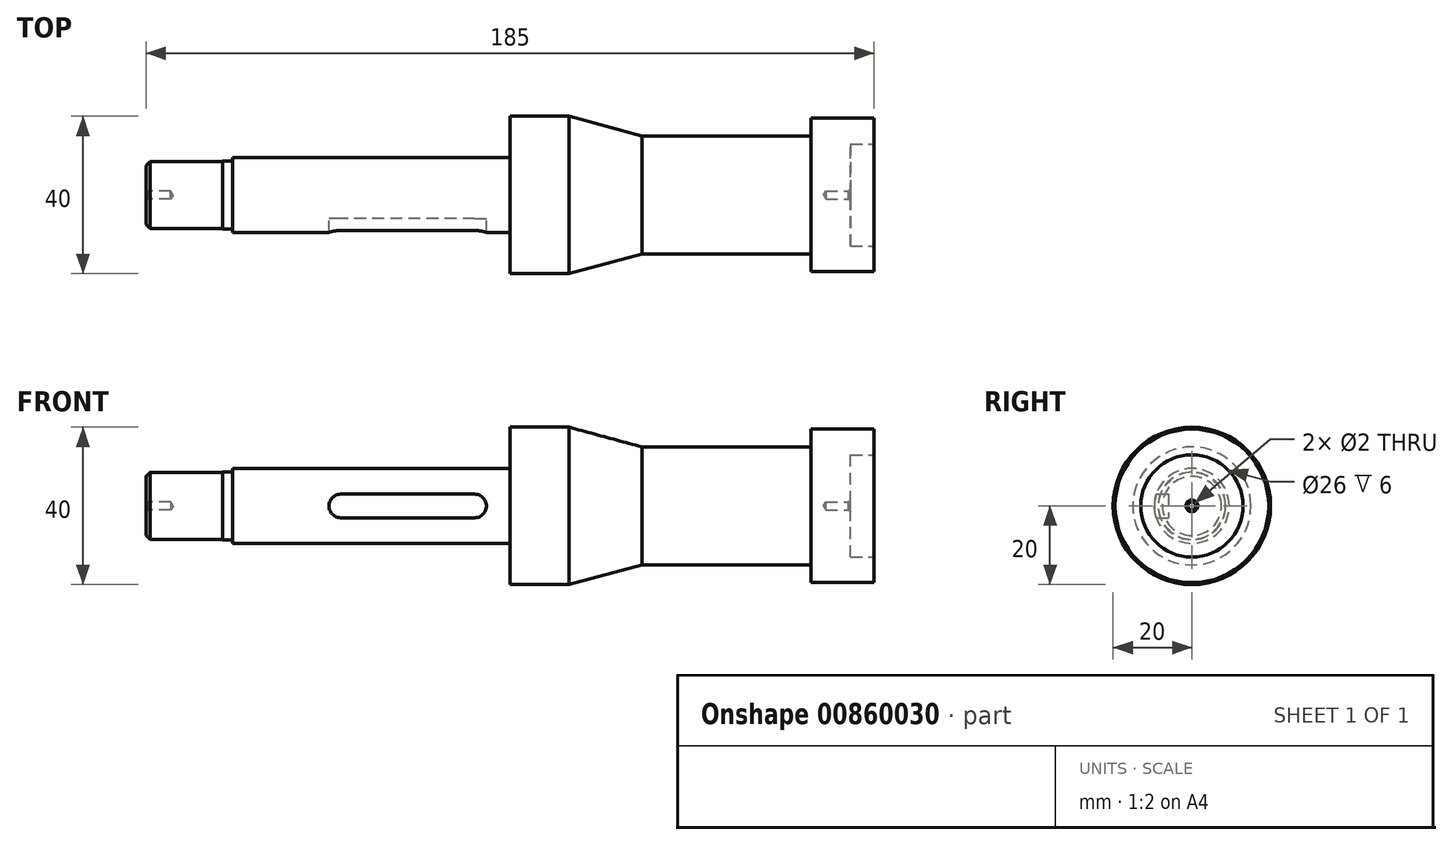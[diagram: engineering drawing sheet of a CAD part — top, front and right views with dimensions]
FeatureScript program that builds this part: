
annotation { "Feature Type Name" : "Feature", "Feature Type Description" : "" }
export const myFeature = defineFeature(function(context is Context, id is Id, definition is map)
    precondition{}
    {
        {
            var Q0;
            Q0=qCreatedBy(makeId("Front.planeOp"),FACE);
            var sketch = newSketch(context, id + "F0", { "sketchPlane" : qUnion([Q0])});
            skLineSegment(sketch, "E0", {"start": v(0, 7.5) * mm, "end": v(1, 8.5) * mm});
            skLineSegment(sketch, "E1", {"start": v(1, 8.5) * mm, "end": v(19.5, 8.5) * mm});
            skLineSegment(sketch, "E2", {"start": v(22, 8.5) * mm, "end": v(22, 9.5) * mm});
            skLineSegment(sketch, "E3", {"start": v(22, 9.5) * mm, "end": v(92.5, 9.5) * mm});
            skLineSegment(sketch, "E4", {"start": v(92.5, 9.5) * mm, "end": v(92.5, 20) * mm});
            skLineSegment(sketch, "E5", {"start": v(92.5, 20) * mm, "end": v(107.5, 20) * mm});
            skLineSegment(sketch, "E6", {"start": v(107.5, 20) * mm, "end": v(126, 15) * mm});
            skLineSegment(sketch, "E7", {"start": v(126, 15) * mm, "end": v(169, 15) * mm});
            skLineSegment(sketch, "E8", {"start": v(169, 15) * mm, "end": v(169, 0) * mm});
            skLineSegment(sketch, "E9", {"start": v(169, 0) * mm, "end": v(0, 0) * mm});
            skLineSegment(sketch, "E10", {"start": v(0, 7.5) * mm, "end": v(0, 0) * mm});
            skLineSegment(sketch, "E11", {"start": v(0, 0) * mm, "end": v(210.6, 0) * mm, "construction": true});
            skLineSegment(sketch, "E12", {"start": v(169, 15) * mm, "end": v(169, 19.5) * mm});
            skLineSegment(sketch, "E13", {"start": v(169, 19.5) * mm, "end": v(185, 19.5) * mm});
            skLineSegment(sketch, "E14", {"start": v(185, 19.5) * mm, "end": v(185, 0) * mm});
            skLineSegment(sketch, "E15", {"start": v(185, 0) * mm, "end": v(169, 0) * mm});
            skLineSegment(sketch, "E16", {"start": v(19.5, 8.5) * mm, "end": v(19.5, 8.6) * mm});
            skLineSegment(sketch, "E17", {"start": v(19.5, 8.6) * mm, "end": v(22, 8.6) * mm});
            skSolve(sketch);
        }
        {
            var Q0;
            Q0 = qSketchRegion(id + "F0", true);
            var Q1;
            Q1=sQuery(id+"F0.wireOp",EDGE,"E11");
            revolve(context, id + "F1", {"surfaceOperationType" : NewSurfaceOperationType.NEW, "entities" : qUnion([Q0]), "axis" : qUnion([Q1]), "revolveType" : RevolveType.FULL});
        }
        {
            var Q0;
            Q0=qCreatedBy(makeId("Front.planeOp"),FACE);
            var sketch = newSketch(context, id + "F2", { "sketchPlane" : qUnion([Q0])});
            skLineSegment(sketch, "E18.bottom", {"start": v(83.5, 3) * mm, "end": v(49.5, 3) * mm});
            skLineSegment(sketch, "E18.top", {"start": v(83.5, -3) * mm, "end": v(49.5, -3) * mm});
            skPoint(sketch, "E18.middle", {"position": v(66.5, 0) * mm});
            skArc(sketch, "E19", {"start": v(49.5, 3) * mm, "mid": v(46.5, 0) * mm, "end": v(49.5, -3) * mm});
            skArc(sketch, "E20", {"start": v(83.5, -3) * mm, "mid": v(86.5, 0) * mm, "end": v(83.5, 3) * mm});
            skSolve(sketch);
        }
        {
            var Q0;
            Q0 = qSketchRegion(id + "F2", true);
            extrude(context, id + "F3", {"entities" : qUnion([Q0]), "operationType" : NewBodyOperationType.REMOVE, "depth" : 15.4 * mm, "offsetDistance" : 25 * mm, "hasSecondDirection" : true, "secondDirectionOppositeDirection" : false, "secondDirectionDepth" : 6 * mm});
        }
        {
            var Q0;
            Q0=makeQuery(id+"F1.opRevolve","SWEPT_FACE",FACE,{"disambiguationData":[OSD([sQuery(id+"F0.wireOp",EDGE,"E14")])]});
            var sketch = newSketch(context, id + "F4", { "sketchPlane" : qUnion([Q0])});
            skCircle(sketch, "E21", {"center": v(0, 0) * mm, "radius": 13 * mm});
            skSolve(sketch);
        }
        {
            var Q0;
            Q0 = qSketchRegion(id + "F4", true);
            extrude(context, id + "F5", {"entities" : qUnion([Q0]), "operationType" : NewBodyOperationType.REMOVE, "oppositeDirection" : true, "depth" : 6 * mm, "offsetDistance" : 25 * mm});
        }
        {
            var Q0;
            Q0=makeQuery(id+"F5.boolean.opBoolean","COPY",FACE,{"derivedFrom":makeQuery(id+"F5.opExtrude","CAP_FACE",FACE,{"disambiguationData":[OSD([sQuery(id+"F4.wireOp",EDGE,"E21")])],"isStart":false})});
            var sketch = newSketch(context, id + "F6", { "sketchPlane" : qUnion([Q0])});
            skPoint(sketch, "E22", {"position": v(0, 0) * mm});
            skSolve(sketch);
        }
        {
            var Q0;
            Q0=makeQuery(id+"F1.opRevolve","SWEPT_FACE",FACE,{"disambiguationData":[OSD([sQuery(id+"F0.wireOp",EDGE,"E10")])]});
            var sketch = newSketch(context, id + "F7", { "sketchPlane" : qUnion([Q0])});
            skPoint(sketch, "E23", {"position": v(0, 0) * mm});
            skSolve(sketch);
        }
        {
            var Q0;
            Q0=sQuery(id+"F7.wireOp",VERTEX,"E23");
            var Q1;
            Q1=sQuery(id+"F6.wireOp",VERTEX,"E22");
            var Q2;
            Q2=makeQuery(id+"F1.opRevolve","SWEPT_BODY",BODY,{"disambiguationData":[OSD([sQuery(id+"F0.wireOp",EDGE,"E0"),sQuery(id+"F0.wireOp",EDGE,"E1"),sQuery(id+"F0.wireOp",EDGE,"E2"),sQuery(id+"F0.wireOp",EDGE,"E3"),sQuery(id+"F0.wireOp",EDGE,"E4"),sQuery(id+"F0.wireOp",EDGE,"E5"),sQuery(id+"F0.wireOp",EDGE,"E6"),sQuery(id+"F0.wireOp",EDGE,"E7"),sQuery(id+"F0.wireOp",EDGE,"E9"),sQuery(id+"F0.wireOp",EDGE,"E10"),sQuery(id+"F0.wireOp",EDGE,"E12"),sQuery(id+"F0.wireOp",EDGE,"E13"),sQuery(id+"F0.wireOp",EDGE,"E14"),sQuery(id+"F0.wireOp",EDGE,"E15")])]});
            hole(context, id + "F8", {"style" : HoleStyle.C_SINK, "endStyle" : HoleEndStyle.BLIND, "holeDiameter" : 2 * mm, "cSinkDiameter" : 3 * mm, "cSinkAngle" : 90 * degree, "majorDiameter" : 5 * mm, "holeDepth" : 6.3 * mm, "isTappedThrough" : true, "tappedDepth" : 3.9 * mm, "tapClearance" : 3, "locations" : qUnion([Q0, Q1]), "scope" : qUnion([Q2])});
        }
    });
